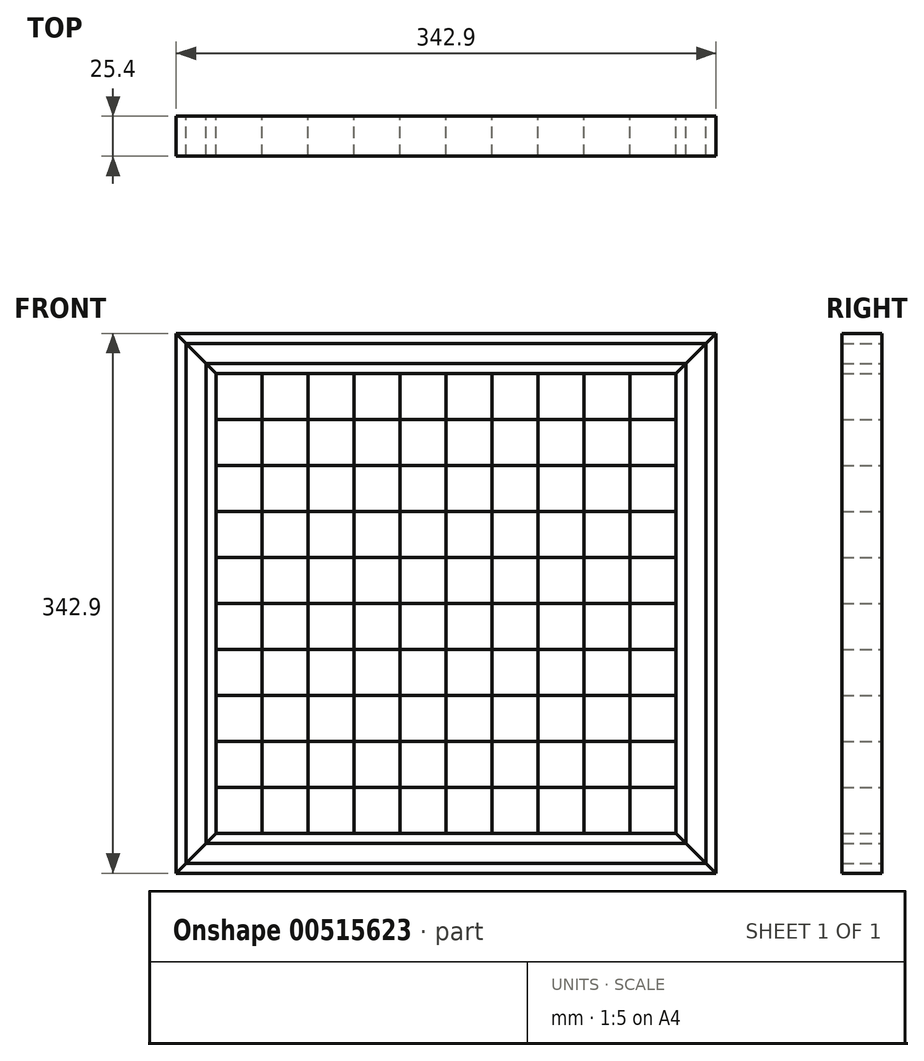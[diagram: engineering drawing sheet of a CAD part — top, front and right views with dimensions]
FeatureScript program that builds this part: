
annotation { "Feature Type Name" : "Feature", "Feature Type Description" : "" }
export const myFeature = defineFeature(function(context is Context, id is Id, definition is map)
    precondition{}
    {
        {
            var Q0;
            Q0=qCreatedBy(makeId("Front.planeOp"),FACE);
            var sketch = newSketch(context, id + "F0", { "sketchPlane" : qUnion([Q0])});
            skLineSegment(sketch, "E0.bottom", {"start": v(171.45, 171.45) * mm, "end": v(-171.45, 171.45) * mm});
            skLineSegment(sketch, "E0.top", {"start": v(171.45, -171.45) * mm, "end": v(-171.45, -171.45) * mm});
            skLineSegment(sketch, "E0.left", {"start": v(171.45, 171.45) * mm, "end": v(171.45, -171.45) * mm});
            skLineSegment(sketch, "E0.right", {"start": v(-171.45, 171.45) * mm, "end": v(-171.45, -171.45) * mm});
            skPoint(sketch, "E0.middle", {"position": v(0, 0) * mm});
            skLineSegment(sketch, "E1.0", {"start": v(146.05, 146.05) * mm, "end": v(116.84, 146.05) * mm});
            skLineSegment(sketch, "E1.1", {"start": v(146.05, 146.05) * mm, "end": v(146.05, -146.05) * mm});
            skLineSegment(sketch, "E1.2", {"start": v(146.05, -146.05) * mm, "end": v(-146.05, -146.05) * mm});
            skLineSegment(sketch, "E1.3", {"start": v(-146.05, 146.05) * mm, "end": v(-146.05, -146.05) * mm});
            skLineSegment(sketch, "E2", {"start": v(-116.84, 146.05) * mm, "end": v(-116.84, -146.05) * mm});
            skLineSegment(sketch, "E3", {"start": v(-87.63, 146.05) * mm, "end": v(-87.63, -146.05) * mm});
            skLineSegment(sketch, "E4", {"start": v(-58.42, 146.05) * mm, "end": v(-58.42, -146.05) * mm});
            skLineSegment(sketch, "E5", {"start": v(-29.2, 146.05) * mm, "end": v(-29.2, -146.05) * mm});
            skLineSegment(sketch, "E6", {"start": v(0, 146.05) * mm, "end": v(0, -146.05) * mm});
            skLineSegment(sketch, "E7", {"start": v(29.21, 146.05) * mm, "end": v(29.21, -146.05) * mm});
            skLineSegment(sketch, "E8", {"start": v(58.42, 146.05) * mm, "end": v(58.42, -146.05) * mm});
            skLineSegment(sketch, "E9", {"start": v(87.63, 146.05) * mm, "end": v(87.63, -146.05) * mm});
            skLineSegment(sketch, "E10", {"start": v(116.84, 146.05) * mm, "end": v(116.84, -146.05) * mm});
            skLineSegment(sketch, "E11.trimOffspring", {"start": v(-87.63, 146.05) * mm, "end": v(-116.84, 146.05) * mm});
            skLineSegment(sketch, "E12.trimOffspring", {"start": v(-29.2, 146.05) * mm, "end": v(-58.42, 146.05) * mm});
            skLineSegment(sketch, "E13.trimOffspring", {"start": v(29.21, 146.05) * mm, "end": v(0, 146.05) * mm});
            skLineSegment(sketch, "E14.trimOffspring", {"start": v(87.63, 146.05) * mm, "end": v(58.42, 146.05) * mm});
            skLineSegment(sketch, "E15", {"start": v(-146.05, 146.05) * mm, "end": v(-116.84, 146.05) * mm});
            skLineSegment(sketch, "E16", {"start": v(-87.63, 146.05) * mm, "end": v(-58.42, 146.05) * mm});
            skLineSegment(sketch, "E17", {"start": v(-29.2, 146.05) * mm, "end": v(0, 146.05) * mm});
            skLineSegment(sketch, "E18", {"start": v(29.21, 146.05) * mm, "end": v(58.42, 146.05) * mm});
            skLineSegment(sketch, "E19", {"start": v(87.63, 146.05) * mm, "end": v(116.84, 146.05) * mm});
            skLineSegment(sketch, "E20.0", {"start": v(146.05, -116.84) * mm, "end": v(-146.05, -116.84) * mm});
            skLineSegment(sketch, "E21.0", {"start": v(146.05, -87.63) * mm, "end": v(-146.05, -87.63) * mm});
            skLineSegment(sketch, "E22.0", {"start": v(146.05, -58.42) * mm, "end": v(-146.05, -58.42) * mm});
            skLineSegment(sketch, "E23.0", {"start": v(146.05, -29.2) * mm, "end": v(-146.05, -29.21) * mm});
            skLineSegment(sketch, "E24.0", {"start": v(146.05, 0) * mm, "end": v(-146.05, 0) * mm});
            skLineSegment(sketch, "E25.MirrorCS", {"start": v(146.05, 29.21) * mm, "end": v(-146.05, 29.2) * mm});
            skLineSegment(sketch, "E26.MirrorCS", {"start": v(146.05, 58.42) * mm, "end": v(-146.05, 58.42) * mm});
            skLineSegment(sketch, "E27.MirrorCS", {"start": v(146.05, 87.63) * mm, "end": v(-146.05, 87.63) * mm});
            skLineSegment(sketch, "E28.MirrorCS", {"start": v(146.05, 116.84) * mm, "end": v(-146.05, 116.84) * mm});
            skLineSegment(sketch, "E29.0", {"start": v(165.1, 165.1) * mm, "end": v(165.1, -165.1) * mm});
            skLineSegment(sketch, "E29.1", {"start": v(165.1, 165.1) * mm, "end": v(-165.1, 165.1) * mm});
            skLineSegment(sketch, "E29.2", {"start": v(-165.1, 165.1) * mm, "end": v(-165.1, -165.1) * mm});
            skLineSegment(sketch, "E29.3", {"start": v(165.1, -165.1) * mm, "end": v(-165.1, -165.1) * mm});
            skLineSegment(sketch, "E30.0", {"start": v(152.4, 152.4) * mm, "end": v(116.84, 152.4) * mm});
            skLineSegment(sketch, "E30.1", {"start": v(87.63, 152.4) * mm, "end": v(116.84, 152.4) * mm});
            skLineSegment(sketch, "E30.2", {"start": v(-87.63, 152.4) * mm, "end": v(-116.84, 152.4) * mm});
            skLineSegment(sketch, "E30.3", {"start": v(-152.4, 152.4) * mm, "end": v(-116.84, 152.4) * mm});
            skLineSegment(sketch, "E30.4", {"start": v(-152.4, 152.4) * mm, "end": v(-152.4, -152.4) * mm});
            skLineSegment(sketch, "E30.5", {"start": v(152.4, -152.4) * mm, "end": v(-152.4, -152.4) * mm});
            skLineSegment(sketch, "E30.6", {"start": v(-87.63, 152.4) * mm, "end": v(-58.42, 152.4) * mm});
            skLineSegment(sketch, "E30.7", {"start": v(-29.2, 152.4) * mm, "end": v(-58.42, 152.4) * mm});
            skLineSegment(sketch, "E30.8", {"start": v(152.4, 152.4) * mm, "end": v(152.4, -152.4) * mm});
            skLineSegment(sketch, "E30.9", {"start": v(-29.2, 152.4) * mm, "end": v(0, 152.4) * mm});
            skLineSegment(sketch, "E30.10", {"start": v(29.21, 152.4) * mm, "end": v(0, 152.4) * mm});
            skLineSegment(sketch, "E30.11", {"start": v(29.21, 152.4) * mm, "end": v(58.42, 152.4) * mm});
            skLineSegment(sketch, "E30.12", {"start": v(87.63, 152.4) * mm, "end": v(58.42, 152.4) * mm});
            skLineSegment(sketch, "E31", {"start": v(-171.45, 171.45) * mm, "end": v(-146.05, 146.05) * mm});
            skLineSegment(sketch, "E32", {"start": v(171.45, 171.45) * mm, "end": v(146.05, 146.05) * mm});
            skLineSegment(sketch, "E33", {"start": v(171.45, -171.45) * mm, "end": v(146.05, -146.05) * mm});
            skLineSegment(sketch, "E34", {"start": v(-146.05, -146.05) * mm, "end": v(-171.45, -171.45) * mm});
            skSolve(sketch);
        }
        {
            var Q0;
            {var subQ0=sQuery(id+"F0.wireOp",EDGE,"E0.bottom");Q0=makeQuery(id+"F0.imprint","IMPRINT",FACE,{"disambiguationData":[TD([[makeQuery(id+"F0.imprint","IMPRINT",EDGE,{"derivedFrom":subQ0}),1.0]])]});}
            var Q1;
            {var subQ1=sQuery(id+"F0.wireOp",EDGE,"E1.0");Q1=makeQuery(id+"F0.imprint","IMPRINT",FACE,{"disambiguationData":[TD([[makeQuery(id+"F0.imprint","IMPRINT",EDGE,{"derivedFrom":subQ1}),-1.0]])]});}
            var Q2;
            {var subQ0=sQuery(id+"F0.wireOp",EDGE,"E29.0");Q2=makeQuery(id+"F0.imprint","IMPRINT",FACE,{"disambiguationData":[TD([[makeQuery(id+"F0.imprint","IMPRINT",EDGE,{"derivedFrom":subQ0}),-1.0]])]});}
            var Q3;
            {var subQ0=sQuery(id+"F0.wireOp",EDGE,"E29.2");Q3=makeQuery(id+"F0.imprint","IMPRINT",FACE,{"disambiguationData":[TD([[makeQuery(id+"F0.imprint","IMPRINT",EDGE,{"derivedFrom":subQ0}),1.0]])]});}
            var Q4;
            {var subQ8=sQuery(id+"F0.wireOp",EDGE,"E30.5");Q4=makeQuery(id+"F0.imprint","IMPRINT",FACE,{"disambiguationData":[TD([[makeQuery(id+"F0.imprint","IMPRINT",EDGE,{"derivedFrom":subQ8}),-1.0]])]});}
            var Q5;
            {var subQ0=sQuery(id+"F0.wireOp",EDGE,"E0.top");Q5=makeQuery(id+"F0.imprint","IMPRINT",FACE,{"disambiguationData":[TD([[makeQuery(id+"F0.imprint","IMPRINT",EDGE,{"derivedFrom":subQ0}),-1.0]])]});}
            var Q6;
            {var subQ0=sQuery(id+"F0.wireOp",EDGE,"E27.MirrorCS");var subQ1=sQuery(id+"F0.wireOp",EDGE,"E1.3");var subQ2=makeQuery(id+"F0.imprint","INTERSECT",VERTEX,{"derivedFrom":[subQ1,subQ0]});Q6=makeQuery(id+"F0.imprint","IMPRINT",FACE,{"disambiguationData":[TD([[makeQuery(id+"F0.imprint","IMPRINT",EDGE,{"disambiguationData":[TD([[subQ2,1.0]])],"derivedFrom":subQ1}),1.0]])]});}
            var Q7;
            {var subQ0=sQuery(id+"F0.wireOp",EDGE,"E25.MirrorCS");var subQ1=sQuery(id+"F0.wireOp",EDGE,"E1.3");var subQ2=makeQuery(id+"F0.imprint","INTERSECT",VERTEX,{"derivedFrom":[subQ1,subQ0]});Q7=makeQuery(id+"F0.imprint","IMPRINT",FACE,{"disambiguationData":[TD([[makeQuery(id+"F0.imprint","IMPRINT",EDGE,{"disambiguationData":[TD([[subQ2,1.0]])],"derivedFrom":subQ1}),1.0]])]});}
            var Q8;
            {var subQ0=sQuery(id+"F0.wireOp",EDGE,"E23.0");var subQ1=sQuery(id+"F0.wireOp",EDGE,"E1.3");var subQ2=makeQuery(id+"F0.imprint","INTERSECT",VERTEX,{"derivedFrom":[subQ1,subQ0]});Q8=makeQuery(id+"F0.imprint","IMPRINT",FACE,{"disambiguationData":[TD([[makeQuery(id+"F0.imprint","IMPRINT",EDGE,{"disambiguationData":[TD([[subQ2,1.0]])],"derivedFrom":subQ1}),1.0]])]});}
            var Q9;
            {var subQ0=sQuery(id+"F0.wireOp",EDGE,"E21.0");var subQ1=sQuery(id+"F0.wireOp",EDGE,"E1.3");var subQ2=makeQuery(id+"F0.imprint","INTERSECT",VERTEX,{"derivedFrom":[subQ1,subQ0]});Q9=makeQuery(id+"F0.imprint","IMPRINT",FACE,{"disambiguationData":[TD([[makeQuery(id+"F0.imprint","IMPRINT",EDGE,{"disambiguationData":[TD([[subQ2,1.0]])],"derivedFrom":subQ1}),1.0]])]});}
            var Q10;
            {var subQ0=sQuery(id+"F0.wireOp",EDGE,"E21.0");var subQ1=sQuery(id+"F0.wireOp",EDGE,"E2");var subQ2=makeQuery(id+"F0.imprint","INTERSECT",VERTEX,{"derivedFrom":[subQ1,subQ0]});Q10=makeQuery(id+"F0.imprint","IMPRINT",FACE,{"disambiguationData":[TD([[makeQuery(id+"F0.imprint","IMPRINT",EDGE,{"disambiguationData":[TD([[subQ2,-1.0]])],"derivedFrom":subQ1}),1.0]])]});}
            var Q11;
            {var subQ0=sQuery(id+"F0.wireOp",EDGE,"E23.0");var subQ1=sQuery(id+"F0.wireOp",EDGE,"E2");var subQ2=makeQuery(id+"F0.imprint","INTERSECT",VERTEX,{"derivedFrom":[subQ1,subQ0]});Q11=makeQuery(id+"F0.imprint","IMPRINT",FACE,{"disambiguationData":[TD([[makeQuery(id+"F0.imprint","IMPRINT",EDGE,{"disambiguationData":[TD([[subQ2,-1.0]])],"derivedFrom":subQ1}),1.0]])]});}
            var Q12;
            {var subQ0=sQuery(id+"F0.wireOp",EDGE,"E25.MirrorCS");var subQ1=sQuery(id+"F0.wireOp",EDGE,"E2");var subQ2=makeQuery(id+"F0.imprint","INTERSECT",VERTEX,{"derivedFrom":[subQ1,subQ0]});Q12=makeQuery(id+"F0.imprint","IMPRINT",FACE,{"disambiguationData":[TD([[makeQuery(id+"F0.imprint","IMPRINT",EDGE,{"disambiguationData":[TD([[subQ2,-1.0]])],"derivedFrom":subQ1}),1.0]])]});}
            var Q13;
            {var subQ0=sQuery(id+"F0.wireOp",EDGE,"E27.MirrorCS");var subQ1=sQuery(id+"F0.wireOp",EDGE,"E2");var subQ2=makeQuery(id+"F0.imprint","INTERSECT",VERTEX,{"derivedFrom":[subQ1,subQ0]});Q13=makeQuery(id+"F0.imprint","IMPRINT",FACE,{"disambiguationData":[TD([[makeQuery(id+"F0.imprint","IMPRINT",EDGE,{"disambiguationData":[TD([[subQ2,-1.0]])],"derivedFrom":subQ1}),1.0]])]});}
            var Q14;
            {var subQ0=sQuery(id+"F0.wireOp",EDGE,"E28.MirrorCS");var subQ1=sQuery(id+"F0.wireOp",EDGE,"E3");var subQ2=makeQuery(id+"F0.imprint","INTERSECT",VERTEX,{"derivedFrom":[subQ1,subQ0]});Q14=makeQuery(id+"F0.imprint","IMPRINT",FACE,{"disambiguationData":[TD([[makeQuery(id+"F0.imprint","IMPRINT",EDGE,{"disambiguationData":[TD([[subQ2,-1.0]])],"derivedFrom":subQ1}),1.0]])]});}
            var Q15;
            {var subQ0=sQuery(id+"F0.wireOp",EDGE,"E26.MirrorCS");var subQ1=sQuery(id+"F0.wireOp",EDGE,"E3");var subQ2=makeQuery(id+"F0.imprint","INTERSECT",VERTEX,{"derivedFrom":[subQ1,subQ0]});Q15=makeQuery(id+"F0.imprint","IMPRINT",FACE,{"disambiguationData":[TD([[makeQuery(id+"F0.imprint","IMPRINT",EDGE,{"disambiguationData":[TD([[subQ2,-1.0]])],"derivedFrom":subQ1}),1.0]])]});}
            var Q16;
            {var subQ0=sQuery(id+"F0.wireOp",EDGE,"E24.0");var subQ1=sQuery(id+"F0.wireOp",EDGE,"E3");var subQ2=makeQuery(id+"F0.imprint","INTERSECT",VERTEX,{"derivedFrom":[subQ1,subQ0]});Q16=makeQuery(id+"F0.imprint","IMPRINT",FACE,{"disambiguationData":[TD([[makeQuery(id+"F0.imprint","IMPRINT",EDGE,{"disambiguationData":[TD([[subQ2,-1.0]])],"derivedFrom":subQ1}),1.0]])]});}
            var Q17;
            {var subQ0=sQuery(id+"F0.wireOp",EDGE,"E22.0");var subQ1=sQuery(id+"F0.wireOp",EDGE,"E3");var subQ2=makeQuery(id+"F0.imprint","INTERSECT",VERTEX,{"derivedFrom":[subQ1,subQ0]});Q17=makeQuery(id+"F0.imprint","IMPRINT",FACE,{"disambiguationData":[TD([[makeQuery(id+"F0.imprint","IMPRINT",EDGE,{"disambiguationData":[TD([[subQ2,-1.0]])],"derivedFrom":subQ1}),1.0]])]});}
            var Q18;
            {var subQ0=sQuery(id+"F0.wireOp",EDGE,"E21.0");var subQ1=sQuery(id+"F0.wireOp",EDGE,"E4");var subQ2=makeQuery(id+"F0.imprint","INTERSECT",VERTEX,{"derivedFrom":[subQ1,subQ0]});Q18=makeQuery(id+"F0.imprint","IMPRINT",FACE,{"disambiguationData":[TD([[makeQuery(id+"F0.imprint","IMPRINT",EDGE,{"disambiguationData":[TD([[subQ2,-1.0]])],"derivedFrom":subQ1}),1.0]])]});}
            var Q19;
            {var subQ0=sQuery(id+"F0.wireOp",EDGE,"E23.0");var subQ1=sQuery(id+"F0.wireOp",EDGE,"E4");var subQ2=makeQuery(id+"F0.imprint","INTERSECT",VERTEX,{"derivedFrom":[subQ1,subQ0]});Q19=makeQuery(id+"F0.imprint","IMPRINT",FACE,{"disambiguationData":[TD([[makeQuery(id+"F0.imprint","IMPRINT",EDGE,{"disambiguationData":[TD([[subQ2,-1.0]])],"derivedFrom":subQ1}),1.0]])]});}
            var Q20;
            {var subQ0=sQuery(id+"F0.wireOp",EDGE,"E25.MirrorCS");var subQ1=sQuery(id+"F0.wireOp",EDGE,"E4");var subQ2=makeQuery(id+"F0.imprint","INTERSECT",VERTEX,{"derivedFrom":[subQ1,subQ0]});Q20=makeQuery(id+"F0.imprint","IMPRINT",FACE,{"disambiguationData":[TD([[makeQuery(id+"F0.imprint","IMPRINT",EDGE,{"disambiguationData":[TD([[subQ2,-1.0]])],"derivedFrom":subQ1}),1.0]])]});}
            var Q21;
            {var subQ0=sQuery(id+"F0.wireOp",EDGE,"E27.MirrorCS");var subQ1=sQuery(id+"F0.wireOp",EDGE,"E4");var subQ2=makeQuery(id+"F0.imprint","INTERSECT",VERTEX,{"derivedFrom":[subQ1,subQ0]});Q21=makeQuery(id+"F0.imprint","IMPRINT",FACE,{"disambiguationData":[TD([[makeQuery(id+"F0.imprint","IMPRINT",EDGE,{"disambiguationData":[TD([[subQ2,-1.0]])],"derivedFrom":subQ1}),1.0]])]});}
            var Q22;
            {var subQ0=sQuery(id+"F0.wireOp",EDGE,"E28.MirrorCS");var subQ1=sQuery(id+"F0.wireOp",EDGE,"E5");var subQ2=makeQuery(id+"F0.imprint","INTERSECT",VERTEX,{"derivedFrom":[subQ1,subQ0]});Q22=makeQuery(id+"F0.imprint","IMPRINT",FACE,{"disambiguationData":[TD([[makeQuery(id+"F0.imprint","IMPRINT",EDGE,{"disambiguationData":[TD([[subQ2,-1.0]])],"derivedFrom":subQ1}),1.0]])]});}
            var Q23;
            {var subQ0=sQuery(id+"F0.wireOp",EDGE,"E26.MirrorCS");var subQ1=sQuery(id+"F0.wireOp",EDGE,"E5");var subQ2=makeQuery(id+"F0.imprint","INTERSECT",VERTEX,{"derivedFrom":[subQ1,subQ0]});Q23=makeQuery(id+"F0.imprint","IMPRINT",FACE,{"disambiguationData":[TD([[makeQuery(id+"F0.imprint","IMPRINT",EDGE,{"disambiguationData":[TD([[subQ2,-1.0]])],"derivedFrom":subQ1}),1.0]])]});}
            var Q24;
            {var subQ0=sQuery(id+"F0.wireOp",EDGE,"E24.0");var subQ1=sQuery(id+"F0.wireOp",EDGE,"E5");var subQ2=makeQuery(id+"F0.imprint","INTERSECT",VERTEX,{"derivedFrom":[subQ1,subQ0]});Q24=makeQuery(id+"F0.imprint","IMPRINT",FACE,{"disambiguationData":[TD([[makeQuery(id+"F0.imprint","IMPRINT",EDGE,{"disambiguationData":[TD([[subQ2,-1.0]])],"derivedFrom":subQ1}),1.0]])]});}
            var Q25;
            {var subQ0=sQuery(id+"F0.wireOp",EDGE,"E22.0");var subQ1=sQuery(id+"F0.wireOp",EDGE,"E5");var subQ2=makeQuery(id+"F0.imprint","INTERSECT",VERTEX,{"derivedFrom":[subQ1,subQ0]});Q25=makeQuery(id+"F0.imprint","IMPRINT",FACE,{"disambiguationData":[TD([[makeQuery(id+"F0.imprint","IMPRINT",EDGE,{"disambiguationData":[TD([[subQ2,-1.0]])],"derivedFrom":subQ1}),1.0]])]});}
            var Q26;
            {var subQ0=sQuery(id+"F0.wireOp",EDGE,"E21.0");var subQ1=sQuery(id+"F0.wireOp",EDGE,"E6");var subQ2=makeQuery(id+"F0.imprint","INTERSECT",VERTEX,{"derivedFrom":[subQ1,subQ0]});Q26=makeQuery(id+"F0.imprint","IMPRINT",FACE,{"disambiguationData":[TD([[makeQuery(id+"F0.imprint","IMPRINT",EDGE,{"disambiguationData":[TD([[subQ2,-1.0]])],"derivedFrom":subQ1}),1.0]])]});}
            var Q27;
            {var subQ0=sQuery(id+"F0.wireOp",EDGE,"E23.0");var subQ1=sQuery(id+"F0.wireOp",EDGE,"E6");var subQ2=makeQuery(id+"F0.imprint","INTERSECT",VERTEX,{"derivedFrom":[subQ1,subQ0]});Q27=makeQuery(id+"F0.imprint","IMPRINT",FACE,{"disambiguationData":[TD([[makeQuery(id+"F0.imprint","IMPRINT",EDGE,{"disambiguationData":[TD([[subQ2,-1.0]])],"derivedFrom":subQ1}),1.0]])]});}
            var Q28;
            {var subQ0=sQuery(id+"F0.wireOp",EDGE,"E25.MirrorCS");var subQ1=sQuery(id+"F0.wireOp",EDGE,"E6");var subQ2=makeQuery(id+"F0.imprint","INTERSECT",VERTEX,{"derivedFrom":[subQ1,subQ0]});Q28=makeQuery(id+"F0.imprint","IMPRINT",FACE,{"disambiguationData":[TD([[makeQuery(id+"F0.imprint","IMPRINT",EDGE,{"disambiguationData":[TD([[subQ2,-1.0]])],"derivedFrom":subQ1}),1.0]])]});}
            var Q29;
            {var subQ0=sQuery(id+"F0.wireOp",EDGE,"E28.MirrorCS");var subQ1=sQuery(id+"F0.wireOp",EDGE,"E7");var subQ2=makeQuery(id+"F0.imprint","INTERSECT",VERTEX,{"derivedFrom":[subQ1,subQ0]});Q29=makeQuery(id+"F0.imprint","IMPRINT",FACE,{"disambiguationData":[TD([[makeQuery(id+"F0.imprint","IMPRINT",EDGE,{"disambiguationData":[TD([[subQ2,-1.0]])],"derivedFrom":subQ1}),1.0]])]});}
            var Q30;
            {var subQ0=sQuery(id+"F0.wireOp",EDGE,"E26.MirrorCS");var subQ1=sQuery(id+"F0.wireOp",EDGE,"E7");var subQ2=makeQuery(id+"F0.imprint","INTERSECT",VERTEX,{"derivedFrom":[subQ1,subQ0]});Q30=makeQuery(id+"F0.imprint","IMPRINT",FACE,{"disambiguationData":[TD([[makeQuery(id+"F0.imprint","IMPRINT",EDGE,{"disambiguationData":[TD([[subQ2,-1.0]])],"derivedFrom":subQ1}),1.0]])]});}
            var Q31;
            {var subQ0=sQuery(id+"F0.wireOp",EDGE,"E24.0");var subQ1=sQuery(id+"F0.wireOp",EDGE,"E7");var subQ2=makeQuery(id+"F0.imprint","INTERSECT",VERTEX,{"derivedFrom":[subQ1,subQ0]});Q31=makeQuery(id+"F0.imprint","IMPRINT",FACE,{"disambiguationData":[TD([[makeQuery(id+"F0.imprint","IMPRINT",EDGE,{"disambiguationData":[TD([[subQ2,-1.0]])],"derivedFrom":subQ1}),1.0]])]});}
            var Q32;
            {var subQ0=sQuery(id+"F0.wireOp",EDGE,"E22.0");var subQ1=sQuery(id+"F0.wireOp",EDGE,"E7");var subQ2=makeQuery(id+"F0.imprint","INTERSECT",VERTEX,{"derivedFrom":[subQ1,subQ0]});Q32=makeQuery(id+"F0.imprint","IMPRINT",FACE,{"disambiguationData":[TD([[makeQuery(id+"F0.imprint","IMPRINT",EDGE,{"disambiguationData":[TD([[subQ2,-1.0]])],"derivedFrom":subQ1}),1.0]])]});}
            var Q33;
            {var subQ0=sQuery(id+"F0.wireOp",EDGE,"E21.0");var subQ1=sQuery(id+"F0.wireOp",EDGE,"E8");var subQ2=makeQuery(id+"F0.imprint","INTERSECT",VERTEX,{"derivedFrom":[subQ1,subQ0]});Q33=makeQuery(id+"F0.imprint","IMPRINT",FACE,{"disambiguationData":[TD([[makeQuery(id+"F0.imprint","IMPRINT",EDGE,{"disambiguationData":[TD([[subQ2,-1.0]])],"derivedFrom":subQ1}),1.0]])]});}
            var Q34;
            {var subQ0=sQuery(id+"F0.wireOp",EDGE,"E25.MirrorCS");var subQ1=sQuery(id+"F0.wireOp",EDGE,"E8");var subQ2=makeQuery(id+"F0.imprint","INTERSECT",VERTEX,{"derivedFrom":[subQ1,subQ0]});Q34=makeQuery(id+"F0.imprint","IMPRINT",FACE,{"disambiguationData":[TD([[makeQuery(id+"F0.imprint","IMPRINT",EDGE,{"disambiguationData":[TD([[subQ2,-1.0]])],"derivedFrom":subQ1}),1.0]])]});}
            var Q35;
            {var subQ0=sQuery(id+"F0.wireOp",EDGE,"E27.MirrorCS");var subQ1=sQuery(id+"F0.wireOp",EDGE,"E8");var subQ2=makeQuery(id+"F0.imprint","INTERSECT",VERTEX,{"derivedFrom":[subQ1,subQ0]});Q35=makeQuery(id+"F0.imprint","IMPRINT",FACE,{"disambiguationData":[TD([[makeQuery(id+"F0.imprint","IMPRINT",EDGE,{"disambiguationData":[TD([[subQ2,-1.0]])],"derivedFrom":subQ1}),1.0]])]});}
            var Q36;
            {var subQ0=sQuery(id+"F0.wireOp",EDGE,"E28.MirrorCS");var subQ1=sQuery(id+"F0.wireOp",EDGE,"E9");var subQ2=makeQuery(id+"F0.imprint","INTERSECT",VERTEX,{"derivedFrom":[subQ1,subQ0]});Q36=makeQuery(id+"F0.imprint","IMPRINT",FACE,{"disambiguationData":[TD([[makeQuery(id+"F0.imprint","IMPRINT",EDGE,{"disambiguationData":[TD([[subQ2,-1.0]])],"derivedFrom":subQ1}),1.0]])]});}
            var Q37;
            {var subQ0=sQuery(id+"F0.wireOp",EDGE,"E26.MirrorCS");var subQ1=sQuery(id+"F0.wireOp",EDGE,"E9");var subQ2=makeQuery(id+"F0.imprint","INTERSECT",VERTEX,{"derivedFrom":[subQ1,subQ0]});Q37=makeQuery(id+"F0.imprint","IMPRINT",FACE,{"disambiguationData":[TD([[makeQuery(id+"F0.imprint","IMPRINT",EDGE,{"disambiguationData":[TD([[subQ2,-1.0]])],"derivedFrom":subQ1}),1.0]])]});}
            var Q38;
            {var subQ0=sQuery(id+"F0.wireOp",EDGE,"E24.0");var subQ1=sQuery(id+"F0.wireOp",EDGE,"E9");var subQ2=makeQuery(id+"F0.imprint","INTERSECT",VERTEX,{"derivedFrom":[subQ1,subQ0]});Q38=makeQuery(id+"F0.imprint","IMPRINT",FACE,{"disambiguationData":[TD([[makeQuery(id+"F0.imprint","IMPRINT",EDGE,{"disambiguationData":[TD([[subQ2,-1.0]])],"derivedFrom":subQ1}),1.0]])]});}
            var Q39;
            {var subQ0=sQuery(id+"F0.wireOp",EDGE,"E22.0");var subQ1=sQuery(id+"F0.wireOp",EDGE,"E9");var subQ2=makeQuery(id+"F0.imprint","INTERSECT",VERTEX,{"derivedFrom":[subQ1,subQ0]});Q39=makeQuery(id+"F0.imprint","IMPRINT",FACE,{"disambiguationData":[TD([[makeQuery(id+"F0.imprint","IMPRINT",EDGE,{"disambiguationData":[TD([[subQ2,-1.0]])],"derivedFrom":subQ1}),1.0]])]});}
            var Q40;
            {var subQ0=sQuery(id+"F0.wireOp",EDGE,"E20.0");var subQ1=sQuery(id+"F0.wireOp",EDGE,"E1.1");var subQ2=makeQuery(id+"F0.imprint","INTERSECT",VERTEX,{"derivedFrom":[subQ1,subQ0]});Q40=makeQuery(id+"F0.imprint","IMPRINT",FACE,{"disambiguationData":[TD([[makeQuery(id+"F0.imprint","IMPRINT",EDGE,{"disambiguationData":[TD([[subQ2,1.0]])],"derivedFrom":subQ1}),-1.0]])]});}
            var Q41;
            {var subQ0=sQuery(id+"F0.wireOp",EDGE,"E22.0");var subQ1=sQuery(id+"F0.wireOp",EDGE,"E1.1");var subQ2=makeQuery(id+"F0.imprint","INTERSECT",VERTEX,{"derivedFrom":[subQ1,subQ0]});Q41=makeQuery(id+"F0.imprint","IMPRINT",FACE,{"disambiguationData":[TD([[makeQuery(id+"F0.imprint","IMPRINT",EDGE,{"disambiguationData":[TD([[subQ2,1.0]])],"derivedFrom":subQ1}),-1.0]])]});}
            var Q42;
            {var subQ0=sQuery(id+"F0.wireOp",EDGE,"E24.0");var subQ1=sQuery(id+"F0.wireOp",EDGE,"E1.1");var subQ2=makeQuery(id+"F0.imprint","INTERSECT",VERTEX,{"derivedFrom":[subQ1,subQ0]});Q42=makeQuery(id+"F0.imprint","IMPRINT",FACE,{"disambiguationData":[TD([[makeQuery(id+"F0.imprint","IMPRINT",EDGE,{"disambiguationData":[TD([[subQ2,1.0]])],"derivedFrom":subQ1}),-1.0]])]});}
            var Q43;
            {var subQ0=sQuery(id+"F0.wireOp",EDGE,"E26.MirrorCS");var subQ1=sQuery(id+"F0.wireOp",EDGE,"E1.1");var subQ2=makeQuery(id+"F0.imprint","INTERSECT",VERTEX,{"derivedFrom":[subQ1,subQ0]});Q43=makeQuery(id+"F0.imprint","IMPRINT",FACE,{"disambiguationData":[TD([[makeQuery(id+"F0.imprint","IMPRINT",EDGE,{"disambiguationData":[TD([[subQ2,1.0]])],"derivedFrom":subQ1}),-1.0]])]});}
            var Q44;
            {var subQ0=sQuery(id+"F0.wireOp",EDGE,"E27.MirrorCS");var subQ1=sQuery(id+"F0.wireOp",EDGE,"E6");var subQ2=makeQuery(id+"F0.imprint","INTERSECT",VERTEX,{"derivedFrom":[subQ1,subQ0]});Q44=makeQuery(id+"F0.imprint","IMPRINT",FACE,{"disambiguationData":[TD([[makeQuery(id+"F0.imprint","IMPRINT",EDGE,{"disambiguationData":[TD([[subQ2,-1.0]])],"derivedFrom":subQ1}),1.0]])]});}
            var Q45;
            {var subQ0=sQuery(id+"F0.wireOp",EDGE,"E23.0");var subQ1=sQuery(id+"F0.wireOp",EDGE,"E8");var subQ2=makeQuery(id+"F0.imprint","INTERSECT",VERTEX,{"derivedFrom":[subQ1,subQ0]});Q45=makeQuery(id+"F0.imprint","IMPRINT",FACE,{"disambiguationData":[TD([[makeQuery(id+"F0.imprint","IMPRINT",EDGE,{"disambiguationData":[TD([[subQ2,-1.0]])],"derivedFrom":subQ1}),1.0]])]});}
            extrude(context, id + "F1", {"entities" : qUnion([Q0, Q1, Q2, Q3, Q4, Q5, Q6, Q7, Q8, Q9, Q10, Q11, Q12, Q13, Q14, Q15, Q16, Q17, Q18, Q19, Q20, Q21, Q22, Q23, Q24, Q25, Q26, Q27, Q28, Q29, Q30, Q31, Q32, Q33, Q34, Q35, Q36, Q37, Q38, Q39, Q40, Q41, Q42, Q43, Q44, Q45]), "depth" : 25.4 * mm, "offsetDistance" : 25.4 * mm});
        }
        {
            var Q0;
            {var subQ0=sQuery(id+"F0.wireOp",EDGE,"E15");Q0=makeQuery(id+"F0.imprint","IMPRINT",FACE,{"disambiguationData":[TD([[makeQuery(id+"F0.imprint","IMPRINT",EDGE,{"derivedFrom":subQ0}),-1.0]])]});}
            var Q1;
            {var subQ0=sQuery(id+"F0.wireOp",EDGE,"E16");Q1=makeQuery(id+"F0.imprint","IMPRINT",FACE,{"disambiguationData":[TD([[makeQuery(id+"F0.imprint","IMPRINT",EDGE,{"derivedFrom":subQ0}),-1.0]])]});}
            var Q2;
            {var subQ0=sQuery(id+"F0.wireOp",EDGE,"E28.MirrorCS");var subQ1=sQuery(id+"F0.wireOp",EDGE,"E4");var subQ2=makeQuery(id+"F0.imprint","INTERSECT",VERTEX,{"derivedFrom":[subQ1,subQ0]});Q2=makeQuery(id+"F0.imprint","IMPRINT",FACE,{"disambiguationData":[TD([[makeQuery(id+"F0.imprint","IMPRINT",EDGE,{"disambiguationData":[TD([[subQ2,-1.0]])],"derivedFrom":subQ1}),1.0]])]});}
            var Q3;
            {var subQ0=sQuery(id+"F0.wireOp",EDGE,"E17");Q3=makeQuery(id+"F0.imprint","IMPRINT",FACE,{"disambiguationData":[TD([[makeQuery(id+"F0.imprint","IMPRINT",EDGE,{"derivedFrom":subQ0}),-1.0]])]});}
            var Q4;
            {var subQ0=sQuery(id+"F0.wireOp",EDGE,"E28.MirrorCS");var subQ1=sQuery(id+"F0.wireOp",EDGE,"E6");var subQ2=makeQuery(id+"F0.imprint","INTERSECT",VERTEX,{"derivedFrom":[subQ1,subQ0]});Q4=makeQuery(id+"F0.imprint","IMPRINT",FACE,{"disambiguationData":[TD([[makeQuery(id+"F0.imprint","IMPRINT",EDGE,{"disambiguationData":[TD([[subQ2,-1.0]])],"derivedFrom":subQ1}),1.0]])]});}
            var Q5;
            {var subQ0=sQuery(id+"F0.wireOp",EDGE,"E18");Q5=makeQuery(id+"F0.imprint","IMPRINT",FACE,{"disambiguationData":[TD([[makeQuery(id+"F0.imprint","IMPRINT",EDGE,{"derivedFrom":subQ0}),-1.0]])]});}
            var Q6;
            {var subQ0=sQuery(id+"F0.wireOp",EDGE,"E28.MirrorCS");var subQ1=sQuery(id+"F0.wireOp",EDGE,"E8");var subQ2=makeQuery(id+"F0.imprint","INTERSECT",VERTEX,{"derivedFrom":[subQ1,subQ0]});Q6=makeQuery(id+"F0.imprint","IMPRINT",FACE,{"disambiguationData":[TD([[makeQuery(id+"F0.imprint","IMPRINT",EDGE,{"disambiguationData":[TD([[subQ2,-1.0]])],"derivedFrom":subQ1}),1.0]])]});}
            var Q7;
            {var subQ0=sQuery(id+"F0.wireOp",EDGE,"E19");Q7=makeQuery(id+"F0.imprint","IMPRINT",FACE,{"disambiguationData":[TD([[makeQuery(id+"F0.imprint","IMPRINT",EDGE,{"derivedFrom":subQ0}),-1.0]])]});}
            var Q8;
            {var subQ0=sQuery(id+"F0.wireOp",EDGE,"E27.MirrorCS");var subQ1=sQuery(id+"F0.wireOp",EDGE,"E1.1");var subQ2=makeQuery(id+"F0.imprint","INTERSECT",VERTEX,{"derivedFrom":[subQ1,subQ0]});Q8=makeQuery(id+"F0.imprint","IMPRINT",FACE,{"disambiguationData":[TD([[makeQuery(id+"F0.imprint","IMPRINT",EDGE,{"disambiguationData":[TD([[subQ2,1.0]])],"derivedFrom":subQ1}),-1.0]])]});}
            var Q9;
            {var subQ0=sQuery(id+"F0.wireOp",EDGE,"E25.MirrorCS");var subQ1=sQuery(id+"F0.wireOp",EDGE,"E1.1");var subQ2=makeQuery(id+"F0.imprint","INTERSECT",VERTEX,{"derivedFrom":[subQ1,subQ0]});Q9=makeQuery(id+"F0.imprint","IMPRINT",FACE,{"disambiguationData":[TD([[makeQuery(id+"F0.imprint","IMPRINT",EDGE,{"disambiguationData":[TD([[subQ2,1.0]])],"derivedFrom":subQ1}),-1.0]])]});}
            var Q10;
            {var subQ0=sQuery(id+"F0.wireOp",EDGE,"E27.MirrorCS");var subQ1=sQuery(id+"F0.wireOp",EDGE,"E9");var subQ2=makeQuery(id+"F0.imprint","INTERSECT",VERTEX,{"derivedFrom":[subQ1,subQ0]});Q10=makeQuery(id+"F0.imprint","IMPRINT",FACE,{"disambiguationData":[TD([[makeQuery(id+"F0.imprint","IMPRINT",EDGE,{"disambiguationData":[TD([[subQ2,-1.0]])],"derivedFrom":subQ1}),1.0]])]});}
            var Q11;
            {var subQ0=sQuery(id+"F0.wireOp",EDGE,"E26.MirrorCS");var subQ1=sQuery(id+"F0.wireOp",EDGE,"E8");var subQ2=makeQuery(id+"F0.imprint","INTERSECT",VERTEX,{"derivedFrom":[subQ1,subQ0]});Q11=makeQuery(id+"F0.imprint","IMPRINT",FACE,{"disambiguationData":[TD([[makeQuery(id+"F0.imprint","IMPRINT",EDGE,{"disambiguationData":[TD([[subQ2,-1.0]])],"derivedFrom":subQ1}),1.0]])]});}
            var Q12;
            {var subQ0=sQuery(id+"F0.wireOp",EDGE,"E27.MirrorCS");var subQ1=sQuery(id+"F0.wireOp",EDGE,"E7");var subQ2=makeQuery(id+"F0.imprint","INTERSECT",VERTEX,{"derivedFrom":[subQ1,subQ0]});Q12=makeQuery(id+"F0.imprint","IMPRINT",FACE,{"disambiguationData":[TD([[makeQuery(id+"F0.imprint","IMPRINT",EDGE,{"disambiguationData":[TD([[subQ2,-1.0]])],"derivedFrom":subQ1}),1.0]])]});}
            var Q13;
            {var subQ0=sQuery(id+"F0.wireOp",EDGE,"E26.MirrorCS");var subQ1=sQuery(id+"F0.wireOp",EDGE,"E6");var subQ2=makeQuery(id+"F0.imprint","INTERSECT",VERTEX,{"derivedFrom":[subQ1,subQ0]});Q13=makeQuery(id+"F0.imprint","IMPRINT",FACE,{"disambiguationData":[TD([[makeQuery(id+"F0.imprint","IMPRINT",EDGE,{"disambiguationData":[TD([[subQ2,-1.0]])],"derivedFrom":subQ1}),1.0]])]});}
            var Q14;
            {var subQ0=sQuery(id+"F0.wireOp",EDGE,"E27.MirrorCS");var subQ1=sQuery(id+"F0.wireOp",EDGE,"E5");var subQ2=makeQuery(id+"F0.imprint","INTERSECT",VERTEX,{"derivedFrom":[subQ1,subQ0]});Q14=makeQuery(id+"F0.imprint","IMPRINT",FACE,{"disambiguationData":[TD([[makeQuery(id+"F0.imprint","IMPRINT",EDGE,{"disambiguationData":[TD([[subQ2,-1.0]])],"derivedFrom":subQ1}),1.0]])]});}
            var Q15;
            {var subQ0=sQuery(id+"F0.wireOp",EDGE,"E26.MirrorCS");var subQ1=sQuery(id+"F0.wireOp",EDGE,"E4");var subQ2=makeQuery(id+"F0.imprint","INTERSECT",VERTEX,{"derivedFrom":[subQ1,subQ0]});Q15=makeQuery(id+"F0.imprint","IMPRINT",FACE,{"disambiguationData":[TD([[makeQuery(id+"F0.imprint","IMPRINT",EDGE,{"disambiguationData":[TD([[subQ2,-1.0]])],"derivedFrom":subQ1}),1.0]])]});}
            var Q16;
            {var subQ0=sQuery(id+"F0.wireOp",EDGE,"E27.MirrorCS");var subQ1=sQuery(id+"F0.wireOp",EDGE,"E3");var subQ2=makeQuery(id+"F0.imprint","INTERSECT",VERTEX,{"derivedFrom":[subQ1,subQ0]});Q16=makeQuery(id+"F0.imprint","IMPRINT",FACE,{"disambiguationData":[TD([[makeQuery(id+"F0.imprint","IMPRINT",EDGE,{"disambiguationData":[TD([[subQ2,-1.0]])],"derivedFrom":subQ1}),1.0]])]});}
            var Q17;
            {var subQ0=sQuery(id+"F0.wireOp",EDGE,"E26.MirrorCS");var subQ1=sQuery(id+"F0.wireOp",EDGE,"E2");var subQ2=makeQuery(id+"F0.imprint","INTERSECT",VERTEX,{"derivedFrom":[subQ1,subQ0]});Q17=makeQuery(id+"F0.imprint","IMPRINT",FACE,{"disambiguationData":[TD([[makeQuery(id+"F0.imprint","IMPRINT",EDGE,{"disambiguationData":[TD([[subQ2,-1.0]])],"derivedFrom":subQ1}),1.0]])]});}
            var Q18;
            {var subQ0=sQuery(id+"F0.wireOp",EDGE,"E26.MirrorCS");var subQ1=sQuery(id+"F0.wireOp",EDGE,"E1.3");var subQ2=makeQuery(id+"F0.imprint","INTERSECT",VERTEX,{"derivedFrom":[subQ1,subQ0]});Q18=makeQuery(id+"F0.imprint","IMPRINT",FACE,{"disambiguationData":[TD([[makeQuery(id+"F0.imprint","IMPRINT",EDGE,{"disambiguationData":[TD([[subQ2,1.0]])],"derivedFrom":subQ1}),1.0]])]});}
            var Q19;
            {var subQ0=sQuery(id+"F0.wireOp",EDGE,"E28.MirrorCS");var subQ1=sQuery(id+"F0.wireOp",EDGE,"E2");var subQ2=makeQuery(id+"F0.imprint","INTERSECT",VERTEX,{"derivedFrom":[subQ1,subQ0]});Q19=makeQuery(id+"F0.imprint","IMPRINT",FACE,{"disambiguationData":[TD([[makeQuery(id+"F0.imprint","IMPRINT",EDGE,{"disambiguationData":[TD([[subQ2,-1.0]])],"derivedFrom":subQ1}),1.0]])]});}
            var Q20;
            {var subQ0=sQuery(id+"F0.wireOp",EDGE,"E24.0");var subQ1=sQuery(id+"F0.wireOp",EDGE,"E1.3");var subQ2=makeQuery(id+"F0.imprint","INTERSECT",VERTEX,{"derivedFrom":[subQ1,subQ0]});Q20=makeQuery(id+"F0.imprint","IMPRINT",FACE,{"disambiguationData":[TD([[makeQuery(id+"F0.imprint","IMPRINT",EDGE,{"disambiguationData":[TD([[subQ2,1.0]])],"derivedFrom":subQ1}),1.0]])]});}
            var Q21;
            {var subQ0=sQuery(id+"F0.wireOp",EDGE,"E25.MirrorCS");var subQ1=sQuery(id+"F0.wireOp",EDGE,"E3");var subQ2=makeQuery(id+"F0.imprint","INTERSECT",VERTEX,{"derivedFrom":[subQ1,subQ0]});Q21=makeQuery(id+"F0.imprint","IMPRINT",FACE,{"disambiguationData":[TD([[makeQuery(id+"F0.imprint","IMPRINT",EDGE,{"disambiguationData":[TD([[subQ2,-1.0]])],"derivedFrom":subQ1}),1.0]])]});}
            var Q22;
            {var subQ0=sQuery(id+"F0.wireOp",EDGE,"E25.MirrorCS");var subQ1=sQuery(id+"F0.wireOp",EDGE,"E5");var subQ2=makeQuery(id+"F0.imprint","INTERSECT",VERTEX,{"derivedFrom":[subQ1,subQ0]});Q22=makeQuery(id+"F0.imprint","IMPRINT",FACE,{"disambiguationData":[TD([[makeQuery(id+"F0.imprint","IMPRINT",EDGE,{"disambiguationData":[TD([[subQ2,-1.0]])],"derivedFrom":subQ1}),1.0]])]});}
            var Q23;
            {var subQ0=sQuery(id+"F0.wireOp",EDGE,"E25.MirrorCS");var subQ1=sQuery(id+"F0.wireOp",EDGE,"E7");var subQ2=makeQuery(id+"F0.imprint","INTERSECT",VERTEX,{"derivedFrom":[subQ1,subQ0]});Q23=makeQuery(id+"F0.imprint","IMPRINT",FACE,{"disambiguationData":[TD([[makeQuery(id+"F0.imprint","IMPRINT",EDGE,{"disambiguationData":[TD([[subQ2,-1.0]])],"derivedFrom":subQ1}),1.0]])]});}
            var Q24;
            {var subQ0=sQuery(id+"F0.wireOp",EDGE,"E25.MirrorCS");var subQ1=sQuery(id+"F0.wireOp",EDGE,"E9");var subQ2=makeQuery(id+"F0.imprint","INTERSECT",VERTEX,{"derivedFrom":[subQ1,subQ0]});Q24=makeQuery(id+"F0.imprint","IMPRINT",FACE,{"disambiguationData":[TD([[makeQuery(id+"F0.imprint","IMPRINT",EDGE,{"disambiguationData":[TD([[subQ2,-1.0]])],"derivedFrom":subQ1}),1.0]])]});}
            var Q25;
            {var subQ0=sQuery(id+"F0.wireOp",EDGE,"E23.0");var subQ1=sQuery(id+"F0.wireOp",EDGE,"E1.1");var subQ2=makeQuery(id+"F0.imprint","INTERSECT",VERTEX,{"derivedFrom":[subQ1,subQ0]});Q25=makeQuery(id+"F0.imprint","IMPRINT",FACE,{"disambiguationData":[TD([[makeQuery(id+"F0.imprint","IMPRINT",EDGE,{"disambiguationData":[TD([[subQ2,1.0]])],"derivedFrom":subQ1}),-1.0]])]});}
            var Q26;
            {var subQ0=sQuery(id+"F0.wireOp",EDGE,"E24.0");var subQ1=sQuery(id+"F0.wireOp",EDGE,"E8");var subQ2=makeQuery(id+"F0.imprint","INTERSECT",VERTEX,{"derivedFrom":[subQ1,subQ0]});Q26=makeQuery(id+"F0.imprint","IMPRINT",FACE,{"disambiguationData":[TD([[makeQuery(id+"F0.imprint","IMPRINT",EDGE,{"disambiguationData":[TD([[subQ2,-1.0]])],"derivedFrom":subQ1}),1.0]])]});}
            var Q27;
            {var subQ0=sQuery(id+"F0.wireOp",EDGE,"E24.0");var subQ1=sQuery(id+"F0.wireOp",EDGE,"E6");var subQ2=makeQuery(id+"F0.imprint","INTERSECT",VERTEX,{"derivedFrom":[subQ1,subQ0]});Q27=makeQuery(id+"F0.imprint","IMPRINT",FACE,{"disambiguationData":[TD([[makeQuery(id+"F0.imprint","IMPRINT",EDGE,{"disambiguationData":[TD([[subQ2,-1.0]])],"derivedFrom":subQ1}),1.0]])]});}
            var Q28;
            {var subQ0=sQuery(id+"F0.wireOp",EDGE,"E24.0");var subQ1=sQuery(id+"F0.wireOp",EDGE,"E4");var subQ2=makeQuery(id+"F0.imprint","INTERSECT",VERTEX,{"derivedFrom":[subQ1,subQ0]});Q28=makeQuery(id+"F0.imprint","IMPRINT",FACE,{"disambiguationData":[TD([[makeQuery(id+"F0.imprint","IMPRINT",EDGE,{"disambiguationData":[TD([[subQ2,-1.0]])],"derivedFrom":subQ1}),1.0]])]});}
            var Q29;
            {var subQ0=sQuery(id+"F0.wireOp",EDGE,"E24.0");var subQ1=sQuery(id+"F0.wireOp",EDGE,"E2");var subQ2=makeQuery(id+"F0.imprint","INTERSECT",VERTEX,{"derivedFrom":[subQ1,subQ0]});Q29=makeQuery(id+"F0.imprint","IMPRINT",FACE,{"disambiguationData":[TD([[makeQuery(id+"F0.imprint","IMPRINT",EDGE,{"disambiguationData":[TD([[subQ2,-1.0]])],"derivedFrom":subQ1}),1.0]])]});}
            var Q30;
            {var subQ0=sQuery(id+"F0.wireOp",EDGE,"E25.MirrorCS");var subQ1=sQuery(id+"F0.wireOp",EDGE,"E3");var subQ2=makeQuery(id+"F0.imprint","INTERSECT",VERTEX,{"derivedFrom":[subQ1,subQ0]});Q30=makeQuery(id+"F0.imprint","IMPRINT",FACE,{"disambiguationData":[TD([[makeQuery(id+"F0.imprint","IMPRINT",EDGE,{"disambiguationData":[TD([[subQ2,-1.0]])],"derivedFrom":subQ1}),1.0]])]});}
            var Q31;
            {var subQ0=sQuery(id+"F0.wireOp",EDGE,"E22.0");var subQ1=sQuery(id+"F0.wireOp",EDGE,"E1.3");var subQ2=makeQuery(id+"F0.imprint","INTERSECT",VERTEX,{"derivedFrom":[subQ1,subQ0]});Q31=makeQuery(id+"F0.imprint","IMPRINT",FACE,{"disambiguationData":[TD([[makeQuery(id+"F0.imprint","IMPRINT",EDGE,{"disambiguationData":[TD([[subQ2,1.0]])],"derivedFrom":subQ1}),1.0]])]});}
            var Q32;
            {var subQ0=sQuery(id+"F0.wireOp",EDGE,"E23.0");var subQ1=sQuery(id+"F0.wireOp",EDGE,"E3");var subQ2=makeQuery(id+"F0.imprint","INTERSECT",VERTEX,{"derivedFrom":[subQ1,subQ0]});Q32=makeQuery(id+"F0.imprint","IMPRINT",FACE,{"disambiguationData":[TD([[makeQuery(id+"F0.imprint","IMPRINT",EDGE,{"disambiguationData":[TD([[subQ2,-1.0]])],"derivedFrom":subQ1}),1.0]])]});}
            var Q33;
            {var subQ0=sQuery(id+"F0.wireOp",EDGE,"E23.0");var subQ1=sQuery(id+"F0.wireOp",EDGE,"E5");var subQ2=makeQuery(id+"F0.imprint","INTERSECT",VERTEX,{"derivedFrom":[subQ1,subQ0]});Q33=makeQuery(id+"F0.imprint","IMPRINT",FACE,{"disambiguationData":[TD([[makeQuery(id+"F0.imprint","IMPRINT",EDGE,{"disambiguationData":[TD([[subQ2,-1.0]])],"derivedFrom":subQ1}),1.0]])]});}
            var Q34;
            {var subQ0=sQuery(id+"F0.wireOp",EDGE,"E23.0");var subQ1=sQuery(id+"F0.wireOp",EDGE,"E7");var subQ2=makeQuery(id+"F0.imprint","INTERSECT",VERTEX,{"derivedFrom":[subQ1,subQ0]});Q34=makeQuery(id+"F0.imprint","IMPRINT",FACE,{"disambiguationData":[TD([[makeQuery(id+"F0.imprint","IMPRINT",EDGE,{"disambiguationData":[TD([[subQ2,-1.0]])],"derivedFrom":subQ1}),1.0]])]});}
            var Q35;
            {var subQ0=sQuery(id+"F0.wireOp",EDGE,"E23.0");var subQ1=sQuery(id+"F0.wireOp",EDGE,"E9");var subQ2=makeQuery(id+"F0.imprint","INTERSECT",VERTEX,{"derivedFrom":[subQ1,subQ0]});Q35=makeQuery(id+"F0.imprint","IMPRINT",FACE,{"disambiguationData":[TD([[makeQuery(id+"F0.imprint","IMPRINT",EDGE,{"disambiguationData":[TD([[subQ2,-1.0]])],"derivedFrom":subQ1}),1.0]])]});}
            var Q36;
            {var subQ0=sQuery(id+"F0.wireOp",EDGE,"E21.0");var subQ1=sQuery(id+"F0.wireOp",EDGE,"E1.1");var subQ2=makeQuery(id+"F0.imprint","INTERSECT",VERTEX,{"derivedFrom":[subQ1,subQ0]});Q36=makeQuery(id+"F0.imprint","IMPRINT",FACE,{"disambiguationData":[TD([[makeQuery(id+"F0.imprint","IMPRINT",EDGE,{"disambiguationData":[TD([[subQ2,1.0]])],"derivedFrom":subQ1}),-1.0]])]});}
            var Q37;
            {var subQ0=sQuery(id+"F0.wireOp",EDGE,"E22.0");var subQ1=sQuery(id+"F0.wireOp",EDGE,"E8");var subQ2=makeQuery(id+"F0.imprint","INTERSECT",VERTEX,{"derivedFrom":[subQ1,subQ0]});Q37=makeQuery(id+"F0.imprint","IMPRINT",FACE,{"disambiguationData":[TD([[makeQuery(id+"F0.imprint","IMPRINT",EDGE,{"disambiguationData":[TD([[subQ2,-1.0]])],"derivedFrom":subQ1}),1.0]])]});}
            var Q38;
            {var subQ0=sQuery(id+"F0.wireOp",EDGE,"E22.0");var subQ1=sQuery(id+"F0.wireOp",EDGE,"E6");var subQ2=makeQuery(id+"F0.imprint","INTERSECT",VERTEX,{"derivedFrom":[subQ1,subQ0]});Q38=makeQuery(id+"F0.imprint","IMPRINT",FACE,{"disambiguationData":[TD([[makeQuery(id+"F0.imprint","IMPRINT",EDGE,{"disambiguationData":[TD([[subQ2,-1.0]])],"derivedFrom":subQ1}),1.0]])]});}
            var Q39;
            {var subQ0=sQuery(id+"F0.wireOp",EDGE,"E22.0");var subQ1=sQuery(id+"F0.wireOp",EDGE,"E4");var subQ2=makeQuery(id+"F0.imprint","INTERSECT",VERTEX,{"derivedFrom":[subQ1,subQ0]});Q39=makeQuery(id+"F0.imprint","IMPRINT",FACE,{"disambiguationData":[TD([[makeQuery(id+"F0.imprint","IMPRINT",EDGE,{"disambiguationData":[TD([[subQ2,-1.0]])],"derivedFrom":subQ1}),1.0]])]});}
            var Q40;
            {var subQ0=sQuery(id+"F0.wireOp",EDGE,"E22.0");var subQ1=sQuery(id+"F0.wireOp",EDGE,"E2");var subQ2=makeQuery(id+"F0.imprint","INTERSECT",VERTEX,{"derivedFrom":[subQ1,subQ0]});Q40=makeQuery(id+"F0.imprint","IMPRINT",FACE,{"disambiguationData":[TD([[makeQuery(id+"F0.imprint","IMPRINT",EDGE,{"disambiguationData":[TD([[subQ2,-1.0]])],"derivedFrom":subQ1}),1.0]])]});}
            var Q41;
            {var subQ0=sQuery(id+"F0.wireOp",EDGE,"E20.0");var subQ1=sQuery(id+"F0.wireOp",EDGE,"E1.3");var subQ2=makeQuery(id+"F0.imprint","INTERSECT",VERTEX,{"derivedFrom":[subQ1,subQ0]});Q41=makeQuery(id+"F0.imprint","IMPRINT",FACE,{"disambiguationData":[TD([[makeQuery(id+"F0.imprint","IMPRINT",EDGE,{"disambiguationData":[TD([[subQ2,1.0]])],"derivedFrom":subQ1}),1.0]])]});}
            var Q42;
            {var subQ0=sQuery(id+"F0.wireOp",EDGE,"E21.0");var subQ1=sQuery(id+"F0.wireOp",EDGE,"E3");var subQ2=makeQuery(id+"F0.imprint","INTERSECT",VERTEX,{"derivedFrom":[subQ1,subQ0]});Q42=makeQuery(id+"F0.imprint","IMPRINT",FACE,{"disambiguationData":[TD([[makeQuery(id+"F0.imprint","IMPRINT",EDGE,{"disambiguationData":[TD([[subQ2,-1.0]])],"derivedFrom":subQ1}),1.0]])]});}
            var Q43;
            {var subQ0=sQuery(id+"F0.wireOp",EDGE,"E21.0");var subQ1=sQuery(id+"F0.wireOp",EDGE,"E5");var subQ2=makeQuery(id+"F0.imprint","INTERSECT",VERTEX,{"derivedFrom":[subQ1,subQ0]});Q43=makeQuery(id+"F0.imprint","IMPRINT",FACE,{"disambiguationData":[TD([[makeQuery(id+"F0.imprint","IMPRINT",EDGE,{"disambiguationData":[TD([[subQ2,-1.0]])],"derivedFrom":subQ1}),1.0]])]});}
            var Q44;
            {var subQ0=sQuery(id+"F0.wireOp",EDGE,"E21.0");var subQ1=sQuery(id+"F0.wireOp",EDGE,"E7");var subQ2=makeQuery(id+"F0.imprint","INTERSECT",VERTEX,{"derivedFrom":[subQ1,subQ0]});Q44=makeQuery(id+"F0.imprint","IMPRINT",FACE,{"disambiguationData":[TD([[makeQuery(id+"F0.imprint","IMPRINT",EDGE,{"disambiguationData":[TD([[subQ2,-1.0]])],"derivedFrom":subQ1}),1.0]])]});}
            var Q45;
            {var subQ0=sQuery(id+"F0.wireOp",EDGE,"E21.0");var subQ1=sQuery(id+"F0.wireOp",EDGE,"E9");var subQ2=makeQuery(id+"F0.imprint","INTERSECT",VERTEX,{"derivedFrom":[subQ1,subQ0]});Q45=makeQuery(id+"F0.imprint","IMPRINT",FACE,{"disambiguationData":[TD([[makeQuery(id+"F0.imprint","IMPRINT",EDGE,{"disambiguationData":[TD([[subQ2,-1.0]])],"derivedFrom":subQ1}),1.0]])]});}
            var Q46;
            {var subQ0=sQuery(id+"F0.wireOp",EDGE,"E1.2");var subQ5=sQuery(id+"F0.wireOp",EDGE,"E10");var subQ6=makeQuery(id+"F0.imprint","INTERSECT",VERTEX,{"derivedFrom":[subQ0,subQ5]});Q46=makeQuery(id+"F0.imprint","IMPRINT",FACE,{"disambiguationData":[TD([[makeQuery(id+"F0.imprint","IMPRINT",EDGE,{"disambiguationData":[TD([[subQ6,1.0]])],"derivedFrom":subQ5}),1.0]])]});}
            var Q47;
            {var subQ0=sQuery(id+"F0.wireOp",EDGE,"E8");var subQ1=sQuery(id+"F0.wireOp",EDGE,"E1.2");var subQ2=makeQuery(id+"F0.imprint","INTERSECT",VERTEX,{"derivedFrom":[subQ1,subQ0]});Q47=makeQuery(id+"F0.imprint","IMPRINT",FACE,{"disambiguationData":[TD([[makeQuery(id+"F0.imprint","IMPRINT",EDGE,{"disambiguationData":[TD([[subQ2,1.0]])],"derivedFrom":subQ1}),-1.0]])]});}
            var Q48;
            {var subQ0=sQuery(id+"F0.wireOp",EDGE,"E6");var subQ1=sQuery(id+"F0.wireOp",EDGE,"E1.2");var subQ2=makeQuery(id+"F0.imprint","INTERSECT",VERTEX,{"derivedFrom":[subQ1,subQ0]});Q48=makeQuery(id+"F0.imprint","IMPRINT",FACE,{"disambiguationData":[TD([[makeQuery(id+"F0.imprint","IMPRINT",EDGE,{"disambiguationData":[TD([[subQ2,1.0]])],"derivedFrom":subQ1}),-1.0]])]});}
            var Q49;
            {var subQ0=sQuery(id+"F0.wireOp",EDGE,"E4");var subQ1=sQuery(id+"F0.wireOp",EDGE,"E1.2");var subQ2=makeQuery(id+"F0.imprint","INTERSECT",VERTEX,{"derivedFrom":[subQ1,subQ0]});Q49=makeQuery(id+"F0.imprint","IMPRINT",FACE,{"disambiguationData":[TD([[makeQuery(id+"F0.imprint","IMPRINT",EDGE,{"disambiguationData":[TD([[subQ2,1.0]])],"derivedFrom":subQ1}),-1.0]])]});}
            var Q50;
            {var subQ0=sQuery(id+"F0.wireOp",EDGE,"E2");var subQ1=sQuery(id+"F0.wireOp",EDGE,"E1.2");var subQ2=makeQuery(id+"F0.imprint","INTERSECT",VERTEX,{"derivedFrom":[subQ1,subQ0]});Q50=makeQuery(id+"F0.imprint","IMPRINT",FACE,{"disambiguationData":[TD([[makeQuery(id+"F0.imprint","IMPRINT",EDGE,{"disambiguationData":[TD([[subQ2,1.0]])],"derivedFrom":subQ1}),-1.0]])]});}
            var Q51;
            {var subQ0=sQuery(id+"F0.wireOp",EDGE,"E29.3");Q51=makeQuery(id+"F0.imprint","IMPRINT",FACE,{"disambiguationData":[TD([[makeQuery(id+"F0.imprint","IMPRINT",EDGE,{"derivedFrom":subQ0}),-1.0]])]});}
            var Q52;
            {var subQ1=sQuery(id+"F0.wireOp",EDGE,"E29.1");Q52=makeQuery(id+"F0.imprint","IMPRINT",FACE,{"disambiguationData":[TD([[makeQuery(id+"F0.imprint","IMPRINT",EDGE,{"derivedFrom":subQ1}),1.0]])]});}
            var Q53;
            {var subQ0=sQuery(id+"F0.wireOp",EDGE,"E0.right");Q53=makeQuery(id+"F0.imprint","IMPRINT",FACE,{"disambiguationData":[TD([[makeQuery(id+"F0.imprint","IMPRINT",EDGE,{"derivedFrom":subQ0}),1.0]])]});}
            var Q54;
            {var subQ0=sQuery(id+"F0.wireOp",EDGE,"E0.left");Q54=makeQuery(id+"F0.imprint","IMPRINT",FACE,{"disambiguationData":[TD([[makeQuery(id+"F0.imprint","IMPRINT",EDGE,{"derivedFrom":subQ0}),-1.0]])]});}
            extrude(context, id + "F2", {"entities" : qUnion([Q0, Q1, Q2, Q3, Q4, Q5, Q6, Q7, Q8, Q9, Q10, Q11, Q12, Q13, Q14, Q15, Q16, Q17, Q18, Q19, Q20, Q21, Q22, Q23, Q24, Q25, Q26, Q27, Q28, Q29, Q30, Q31, Q32, Q33, Q34, Q35, Q36, Q37, Q38, Q39, Q40, Q41, Q42, Q43, Q44, Q45, Q46, Q47, Q48, Q49, Q50, Q51, Q52, Q53, Q54]), "depth" : 25.4 * mm, "offsetDistance" : 25.4 * mm});
        }
        {
            var Q0;
            {var subQ0=sQuery(id+"F0.wireOp",EDGE,"E11.trimOffspring");Q0=makeQuery(id+"F0.imprint","IMPRINT",FACE,{"disambiguationData":[TD([[makeQuery(id+"F0.imprint","IMPRINT",EDGE,{"derivedFrom":subQ0}),1.0]])]});}
            var Q1;
            {var subQ0=sQuery(id+"F0.wireOp",EDGE,"E12.trimOffspring");Q1=makeQuery(id+"F0.imprint","IMPRINT",FACE,{"disambiguationData":[TD([[makeQuery(id+"F0.imprint","IMPRINT",EDGE,{"derivedFrom":subQ0}),1.0]])]});}
            var Q2;
            {var subQ0=sQuery(id+"F0.wireOp",EDGE,"E13.trimOffspring");Q2=makeQuery(id+"F0.imprint","IMPRINT",FACE,{"disambiguationData":[TD([[makeQuery(id+"F0.imprint","IMPRINT",EDGE,{"derivedFrom":subQ0}),1.0]])]});}
            var Q3;
            {var subQ0=sQuery(id+"F0.wireOp",EDGE,"E14.trimOffspring");Q3=makeQuery(id+"F0.imprint","IMPRINT",FACE,{"disambiguationData":[TD([[makeQuery(id+"F0.imprint","IMPRINT",EDGE,{"derivedFrom":subQ0}),1.0]])]});}
            var Q4;
            {var subQ0=sQuery(id+"F0.wireOp",EDGE,"E1.0");Q4=makeQuery(id+"F0.imprint","IMPRINT",FACE,{"disambiguationData":[TD([[makeQuery(id+"F0.imprint","IMPRINT",EDGE,{"derivedFrom":subQ0}),1.0]])]});}
            var Q5;
            {var subQ0=sQuery(id+"F0.wireOp",EDGE,"E9");var subQ1=sQuery(id+"F0.wireOp",EDGE,"E1.2");var subQ2=makeQuery(id+"F0.imprint","INTERSECT",VERTEX,{"derivedFrom":[subQ1,subQ0]});Q5=makeQuery(id+"F0.imprint","IMPRINT",FACE,{"disambiguationData":[TD([[makeQuery(id+"F0.imprint","IMPRINT",EDGE,{"disambiguationData":[TD([[subQ2,1.0]])],"derivedFrom":subQ1}),-1.0]])]});}
            var Q6;
            {var subQ0=sQuery(id+"F0.wireOp",EDGE,"E7");var subQ1=sQuery(id+"F0.wireOp",EDGE,"E1.2");var subQ2=makeQuery(id+"F0.imprint","INTERSECT",VERTEX,{"derivedFrom":[subQ1,subQ0]});Q6=makeQuery(id+"F0.imprint","IMPRINT",FACE,{"disambiguationData":[TD([[makeQuery(id+"F0.imprint","IMPRINT",EDGE,{"disambiguationData":[TD([[subQ2,1.0]])],"derivedFrom":subQ1}),-1.0]])]});}
            var Q7;
            {var subQ0=sQuery(id+"F0.wireOp",EDGE,"E5");var subQ1=sQuery(id+"F0.wireOp",EDGE,"E1.2");var subQ2=makeQuery(id+"F0.imprint","INTERSECT",VERTEX,{"derivedFrom":[subQ1,subQ0]});Q7=makeQuery(id+"F0.imprint","IMPRINT",FACE,{"disambiguationData":[TD([[makeQuery(id+"F0.imprint","IMPRINT",EDGE,{"disambiguationData":[TD([[subQ2,1.0]])],"derivedFrom":subQ1}),-1.0]])]});}
            var Q8;
            {var subQ0=sQuery(id+"F0.wireOp",EDGE,"E3");var subQ1=sQuery(id+"F0.wireOp",EDGE,"E1.2");var subQ2=makeQuery(id+"F0.imprint","INTERSECT",VERTEX,{"derivedFrom":[subQ1,subQ0]});Q8=makeQuery(id+"F0.imprint","IMPRINT",FACE,{"disambiguationData":[TD([[makeQuery(id+"F0.imprint","IMPRINT",EDGE,{"disambiguationData":[TD([[subQ2,1.0]])],"derivedFrom":subQ1}),-1.0]])]});}
            var Q9;
            {var subQ1=sQuery(id+"F0.wireOp",EDGE,"E1.2");var subQ3=sQuery(id+"F0.wireOp",EDGE,"E2");var subQ4=makeQuery(id+"F0.imprint","INTERSECT",VERTEX,{"derivedFrom":[subQ1,subQ3]});Q9=makeQuery(id+"F0.imprint","IMPRINT",FACE,{"disambiguationData":[TD([[makeQuery(id+"F0.imprint","IMPRINT",EDGE,{"disambiguationData":[TD([[subQ4,1.0]])],"derivedFrom":subQ3}),-1.0]])]});}
            extrude(context, id + "F3", {"entities" : qUnion([Q0, Q1, Q2, Q3, Q4, Q5, Q6, Q7, Q8, Q9]), "depth" : 25.4 * mm, "offsetDistance" : 25.4 * mm});
        }
        {
            var Q0;
            {var subQ12=sQuery(id+"F0.wireOp",EDGE,"E30.4");Q0=makeQuery(id+"F0.imprint","IMPRINT",FACE,{"disambiguationData":[TD([[makeQuery(id+"F0.imprint","IMPRINT",EDGE,{"derivedFrom":subQ12}),1.0]])]});}
            var Q1;
            {var subQ13=sQuery(id+"F0.wireOp",EDGE,"E30.8");Q1=makeQuery(id+"F0.imprint","IMPRINT",FACE,{"disambiguationData":[TD([[makeQuery(id+"F0.imprint","IMPRINT",EDGE,{"derivedFrom":subQ13}),-1.0]])]});}
            extrude(context, id + "F4", {"entities" : qUnion([Q0, Q1]), "depth" : 25.4 * mm, "offsetDistance" : 25.4 * mm});
        }
    });
